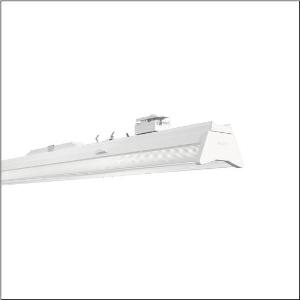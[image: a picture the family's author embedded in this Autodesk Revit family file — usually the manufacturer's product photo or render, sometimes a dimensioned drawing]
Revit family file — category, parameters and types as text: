
# Revit family: licross_21_performance_mo_52tm16cn445g
name_source: partatom
category: Lighting Fixtures
units: mm (PartAtom-declared; Revit-internal decimal feet)

## family parameters
Cut with Voids When Loaded = No
Host = Face
Light Source = No
Part Type = Normal
Room Calculation Point = No
Round Connector Dimension = Use Diameter
Shared = No

## types (1)
- --- (1 x LED, 4500 lm, 24.1 W, 4000K)
    Apparent Load = 24 VA
    CIE Flux Codes = 66 88 96 79 100
    Color Rendering = 80
    Color Temperature = 4000K
    Default Elevation = 1800 mm
    Description = Licross 21 Performance MO, luminaire insert, of sheet steel, galvanised, coil coated, white, length: 1.500mm, width: 120mm, height: 123mm, LED rated luminous flux: 4.500lm, light colour: 840, SDCM (Standard Deviation of Colour Matching)MacAdam ≤ 3 SDCM (initial), control gear: ON/OFF Multilumen, CLOi, with plug, 3-pole, with phase selection, mains connection: 220..240V, AC, 50/60Hz, start of lifetime: 24W, end of service life: 28W, internal wiring halogen-free, primary light control with lens, of plastic, primary optical cover: cover, of PMMA, CAT 2 (L<= 3000cd/m²), light emission: direct/indirect distribution, primary light characteristic: symmetric, protection rating (complete): IP40, insulation class (complete): insulation class I (protective earthing), certification: CE, ENEC, UKCA, protection symbol: D if used in an environment without relevant dust loads with corresponding accessories, impact resistance: IK06, permissible ambient temperature for indoor applications: -35..+55°C, corresponds to IFS (International Featured Standards) requirements for safety and quality in the food industry, reducing of maximum allowable ambient temperature of 5°C with ceiling mounting, LABS conformity tested according to VDMA 24364:2018-05, The light source and the operating device comply with the requirements of the Ecodesign Regulation (EU) 2019/2020 and are replaceable in accordance with this regulation, packaging unit: 1 piece
    Height = 114 mm
    Lamp = 1 x LED
    Lamp Light Flux = 4500 lm
    Lamp Power = 24.1 W
    Lamp count = 1
    Length = 1500 mm
    Luminous efficacy = 187 lm/W
    Manufacturer = Siteco
    ModVariant = No
    Model = 52TM16CN445G
    Mounting Place = Ceiling
    Mounting Type = Pendant
    Number of Poles = 1
    OnlyDefault = Yes
    Power Factor = 1
    Product Name = Licross 21 Performance MO
    Product group = luminaire insert | ceiling pendant
    ProductGroupID = 901
    Protection Class = Protection class I
    Protection Degree = IP 40
    RLX_Detail_Level = 1
    RLX_Emergency_Light_Flux = 0 lm
    RLX_Emergency_Type = 0
    RLX_Emergency_Type_DB = No
    RlxData = <blob elided: 31733 chars, md5=d0f8476f>
    Socket = socket
    Standby Power = 0 W
    System Light Flux = 4500 lm
    System Power = 24 W
    Type Comments = factory setting: luminous flux: 100 % | (A | C | E) | 55 mA
    Type Image = l_1256138.jpg
    URL = http://relux.com
    VarID = @adj_057871
    Voltage = 0 V
    Weight = 0.00 kg
    Width = 120 mm

## geometry (parser evidence)
native form markers: Blend x4, Sweep x11
no freeform markers — native parametric forms only
